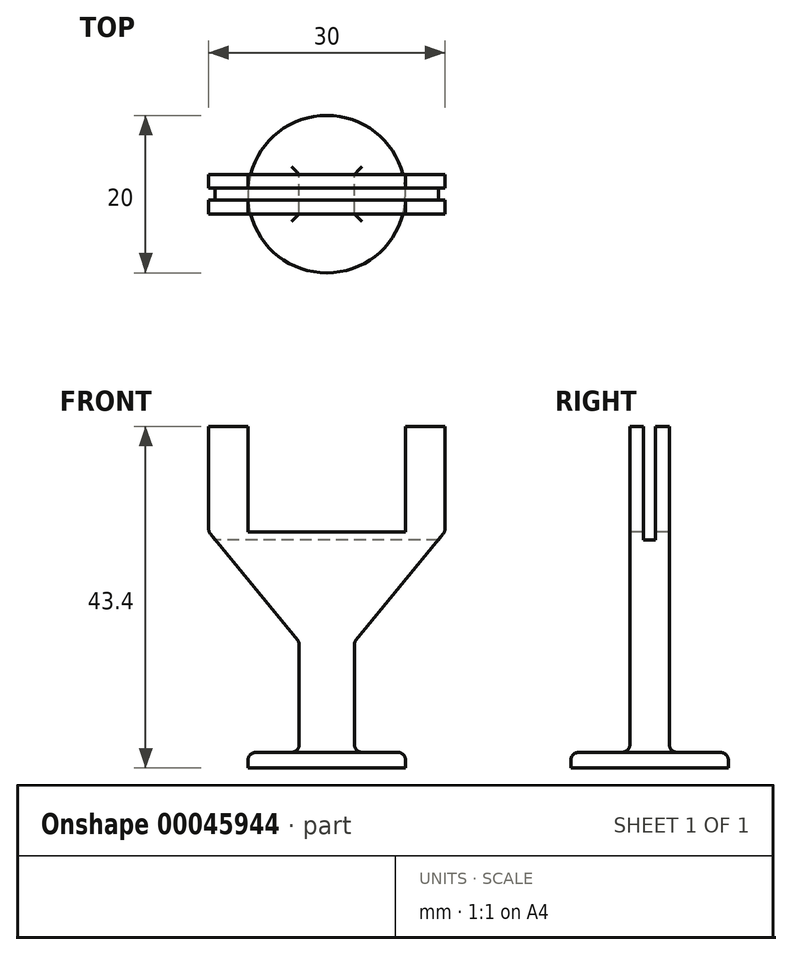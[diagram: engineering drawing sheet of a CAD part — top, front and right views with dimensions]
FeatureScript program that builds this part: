
annotation { "Feature Type Name" : "Feature", "Feature Type Description" : "" }
export const myFeature = defineFeature(function(context is Context, id is Id, definition is map)
    precondition{}
    {
        {
            var Q0;
            Q0=qCreatedBy(makeId("Top.planeOp"),FACE);
            var sketch = newSketch(context, id + "F0", { "sketchPlane" : qUnion([Q0])});
            skCircle(sketch, "E0", {"center": v(0, 0) * mm, "radius": 10 * mm});
            skSolve(sketch);
        }
        {
            var Q0;
            Q0=makeQuery(id+"F0.imprint","IMPRINT",FACE,{"disambiguationData":[TD([[makeQuery(id+"F0.imprint","IMPRINT",EDGE,{"derivedFrom":sQuery(id+"F0.wireOp",EDGE,"E0")}),1.0]])]});
            extrude(context, id + "F1", {"entities" : qUnion([Q0]), "depth" : 2 * mm});
        }
        {
            var Q0;
            Q0=qCreatedBy(makeId("Front.planeOp"),FACE);
            var sketch = newSketch(context, id + "F2", { "sketchPlane" : qUnion([Q0])});
            skLineSegment(sketch, "E1", {"start": v(0, 0) * mm, "end": v(0, 45) * mm, "construction": true});
            skLineSegment(sketch, "E2", {"start": v(-3.5, 30) * mm, "end": v(3.5, 30) * mm, "construction": true});
            skLineSegment(sketch, "E3.0", {"start": v(-10, 2) * mm, "end": v(10, 2) * mm, "construction": true});
            skLineSegment(sketch, "E4", {"start": v(-3.5, 30) * mm, "end": v(-3.5, 2) * mm});
            skLineSegment(sketch, "E5.MirrorCS", {"start": v(3.5, 30) * mm, "end": v(3.5, 2) * mm});
            skLineSegment(sketch, "E6", {"start": v(-3.5, 2) * mm, "end": v(3.5, 2) * mm});
            skLineSegment(sketch, "E7.rect.bottom", {"start": v(15, 30) * mm, "end": v(-15, 30) * mm});
            skLineSegment(sketch, "E7.rect.top", {"start": v(15, 60) * mm, "end": v(-15, 60) * mm});
            skLineSegment(sketch, "E7.rect.left", {"start": v(15, 30) * mm, "end": v(15, 60) * mm});
            skLineSegment(sketch, "E7.rect.right", {"start": v(-15, 30) * mm, "end": v(-15, 60) * mm});
            skPoint(sketch, "E7.rect.middle", {"position": v(0, 45) * mm});
            skLineSegment(sketch, "E8", {"start": v(-15, 30) * mm, "end": v(-3.5, 16) * mm});
            skLineSegment(sketch, "E9.MirrorCS", {"start": v(15, 30) * mm, "end": v(3.5, 16) * mm});
            skSolve(sketch);
        }
        {
            var Q0;
            Q0 = qSketchRegion(id + "F2", true);
            extrude(context, id + "F3", {"entities" : qUnion([Q0]), "operationType" : NewBodyOperationType.ADD, "endBound" : BoundingType.SYMMETRIC, "depth" : 5 * mm});
        }
        {
            var Q0;
            Q0=makeQuery(id+"F3.opExtrude","CAP_FACE",FACE,{"disambiguationData":[OSD([sQuery(id+"F2.wireOp",EDGE,"E4"),sQuery(id+"F2.wireOp",EDGE,"E5.MirrorCS"),sQuery(id+"F2.wireOp",EDGE,"E6"),sQuery(id+"F2.wireOp",EDGE,"E7.rect.top"),sQuery(id+"F2.wireOp",EDGE,"E7.rect.left"),sQuery(id+"F2.wireOp",EDGE,"E7.rect.right"),sQuery(id+"F2.wireOp",EDGE,"E8"),sQuery(id+"F2.wireOp",EDGE,"E9.MirrorCS")])],"isStart":false});
            var sketch = newSketch(context, id + "F4", { "sketchPlane" : qUnion([Q0])});
            skPoint(sketch, "E10.0", {"position": v(0, 45) * mm});
            skLineSegment(sketch, "E11.rect.bottom", {"start": v(10, 60) * mm, "end": v(-10, 60) * mm});
            skLineSegment(sketch, "E11.rect.top", {"start": v(10, 30) * mm, "end": v(-10, 30) * mm});
            skLineSegment(sketch, "E11.rect.left", {"start": v(10, 60) * mm, "end": v(10, 30) * mm});
            skLineSegment(sketch, "E11.rect.right", {"start": v(-10, 60) * mm, "end": v(-10, 30) * mm});
            skSolve(sketch);
        }
        {
            var Q0;
            Q0 = qSketchRegion(id + "F4", true);
            extrude(context, id + "F5", {"entities" : qUnion([Q0]), "operationType" : NewBodyOperationType.REMOVE, "endBound" : BoundingType.THROUGH_ALL, "oppositeDirection" : true, "depth" : 25 * mm});
        }
        {
            var Q0;
            {var subQ0=sQuery(id+"F2.wireOp",EDGE,"E7.rect.top");var subQ1=sQuery(id+"F2.wireOp",EDGE,"E7.rect.right");Q0=makeQuery(id+"F5.boolean.opBoolean","SPLIT",FACE,{"disambiguationData":[TD([makeQuery(id+"F3.opExtrude","SWEPT_FACE",FACE,{"disambiguationData":[OSD([subQ1])]})])],"derivedFrom":makeQuery(id+"F3.opExtrude","SWEPT_FACE",FACE,{"disambiguationData":[OSD([subQ0])]})});}
            var sketch = newSketch(context, id + "F6", { "sketchPlane" : qUnion([Q0])});
            skLineSegment(sketch, "E12.rect.bottom", {"start": v(15, -0.75) * mm, "end": v(-15, -0.75) * mm});
            skLineSegment(sketch, "E12.rect.top", {"start": v(15, 0.75) * mm, "end": v(-15, 0.75) * mm});
            skLineSegment(sketch, "E12.rect.left", {"start": v(15, -0.75) * mm, "end": v(15, 0.75) * mm});
            skLineSegment(sketch, "E12.rect.right", {"start": v(-15, -0.75) * mm, "end": v(-15, 0.75) * mm});
            skPoint(sketch, "E12.rect.middle", {"position": v(0, 0) * mm});
            skSolve(sketch);
        }
        {
            var Q0;
            Q0 = qSketchRegion(id + "F6", true);
            extrude(context, id + "F7", {"entities" : qUnion([Q0]), "operationType" : NewBodyOperationType.REMOVE, "oppositeDirection" : true, "depth" : 31 * mm});
        }
        {
            var Q0;
            Q0=makeQuery(id+"F3.opExtrude","CAP_FACE",FACE,{"disambiguationData":[OSD([sQuery(id+"F2.wireOp",EDGE,"E4"),sQuery(id+"F2.wireOp",EDGE,"E5.MirrorCS"),sQuery(id+"F2.wireOp",EDGE,"E6"),sQuery(id+"F2.wireOp",EDGE,"E7.rect.top"),sQuery(id+"F2.wireOp",EDGE,"E7.rect.left"),sQuery(id+"F2.wireOp",EDGE,"E7.rect.right"),sQuery(id+"F2.wireOp",EDGE,"E8"),sQuery(id+"F2.wireOp",EDGE,"E9.MirrorCS")])],"isStart":false});
            var sketch = newSketch(context, id + "F8", { "sketchPlane" : qUnion([Q0])});
            skLineSegment(sketch, "E13.bottom", {"start": v(-15, 43.4) * mm, "end": v(15, 43.4) * mm});
            skLineSegment(sketch, "E13.top", {"start": v(-15, 60) * mm, "end": v(15, 60) * mm});
            skLineSegment(sketch, "E13.left", {"start": v(-15, 43.4) * mm, "end": v(-15, 60) * mm});
            skLineSegment(sketch, "E13.right", {"start": v(15, 43.4) * mm, "end": v(15, 60) * mm});
            skSolve(sketch);
        }
        {
            var Q0;
            Q0 = qSketchRegion(id + "F8", true);
            extrude(context, id + "F9", {"entities" : qUnion([Q0]), "operationType" : NewBodyOperationType.REMOVE, "endBound" : BoundingType.THROUGH_ALL, "oppositeDirection" : true, "depth" : 25 * mm});
        }
        {
            var Q0;
            Q0=makeQuery(id+"F1.opExtrude","CAP_EDGE",EDGE,{"disambiguationData":[OSD([sQuery(id+"F0.wireOp",EDGE,"E0")])],"isStart":false});
            var Q1;
            Q1=makeQuery(id+"F1.opExtrude","CAP_FACE",FACE,{"disambiguationData":[OSD([sQuery(id+"F0.wireOp",EDGE,"E0")])],"isStart":false});
            var Q2;
            Q2=makeQuery(id+"F3.opExtrude","SWEPT_EDGE",EDGE,{"disambiguationData":[OSD([sQuery(id+"F2.wireOp",EDGE,"E4"),sQuery(id+"F2.wireOp",EDGE,"E8")])]});
            var Q3;
            Q3=makeQuery(id+"F3.opExtrude","SWEPT_EDGE",EDGE,{"disambiguationData":[OSD([sQuery(id+"F2.wireOp",EDGE,"E5.MirrorCS"),sQuery(id+"F2.wireOp",EDGE,"E9.MirrorCS")])]});
            var Q4;
            {var subQ0=sQuery(id+"F2.wireOp",EDGE,"E7.rect.left");var subQ1=sQuery(id+"F2.wireOp",EDGE,"E9.MirrorCS");Q4=makeQuery(id+"F7.boolean.opBoolean","SPLIT",EDGE,{"disambiguationData":[TD([makeQuery(id+"F7.opExtrude","SWEPT_FACE",FACE,{"disambiguationData":[OSD([sQuery(id+"F6.wireOp",EDGE,"E12.rect.bottom")])]})])],"derivedFrom":makeQuery(id+"F3.opExtrude","SWEPT_EDGE",EDGE,{"disambiguationData":[OSD([sQuery(id+"F2.wireOp",EDGE,"E7.rect.bottom"),subQ0,subQ1])]})});}
            var Q5;
            {var subQ0=sQuery(id+"F2.wireOp",EDGE,"E7.rect.left");var subQ1=sQuery(id+"F2.wireOp",EDGE,"E9.MirrorCS");Q5=makeQuery(id+"F7.boolean.opBoolean","SPLIT",EDGE,{"disambiguationData":[TD([makeQuery(id+"F7.opExtrude","SWEPT_FACE",FACE,{"disambiguationData":[OSD([sQuery(id+"F6.wireOp",EDGE,"E12.rect.top")])]})])],"derivedFrom":makeQuery(id+"F3.opExtrude","SWEPT_EDGE",EDGE,{"disambiguationData":[OSD([sQuery(id+"F2.wireOp",EDGE,"E7.rect.bottom"),subQ0,subQ1])]})});}
            var Q6;
            {var subQ0=sQuery(id+"F2.wireOp",EDGE,"E7.rect.right");var subQ1=sQuery(id+"F2.wireOp",EDGE,"E8");Q6=makeQuery(id+"F7.boolean.opBoolean","SPLIT",EDGE,{"disambiguationData":[TD([makeQuery(id+"F7.opExtrude","SWEPT_FACE",FACE,{"disambiguationData":[OSD([sQuery(id+"F6.wireOp",EDGE,"E12.rect.bottom")])]})])],"derivedFrom":makeQuery(id+"F3.opExtrude","SWEPT_EDGE",EDGE,{"disambiguationData":[OSD([sQuery(id+"F2.wireOp",EDGE,"E7.rect.bottom"),subQ0,subQ1])]})});}
            var Q7;
            {var subQ0=sQuery(id+"F2.wireOp",EDGE,"E7.rect.right");var subQ1=sQuery(id+"F2.wireOp",EDGE,"E8");Q7=makeQuery(id+"F7.boolean.opBoolean","SPLIT",EDGE,{"disambiguationData":[TD([makeQuery(id+"F7.opExtrude","SWEPT_FACE",FACE,{"disambiguationData":[OSD([sQuery(id+"F6.wireOp",EDGE,"E12.rect.top")])]})])],"derivedFrom":makeQuery(id+"F3.opExtrude","SWEPT_EDGE",EDGE,{"disambiguationData":[OSD([sQuery(id+"F2.wireOp",EDGE,"E7.rect.bottom"),subQ0,subQ1])]})});}
            fillet(context, id + "F10", {"entities" : qUnion([Q0, Q1, Q2, Q3, Q4, Q5, Q6, Q7]), "radius" : 1 * mm, "tangentPropagation" : true, "allowEdgeOverflow" : false});
        }
    });
